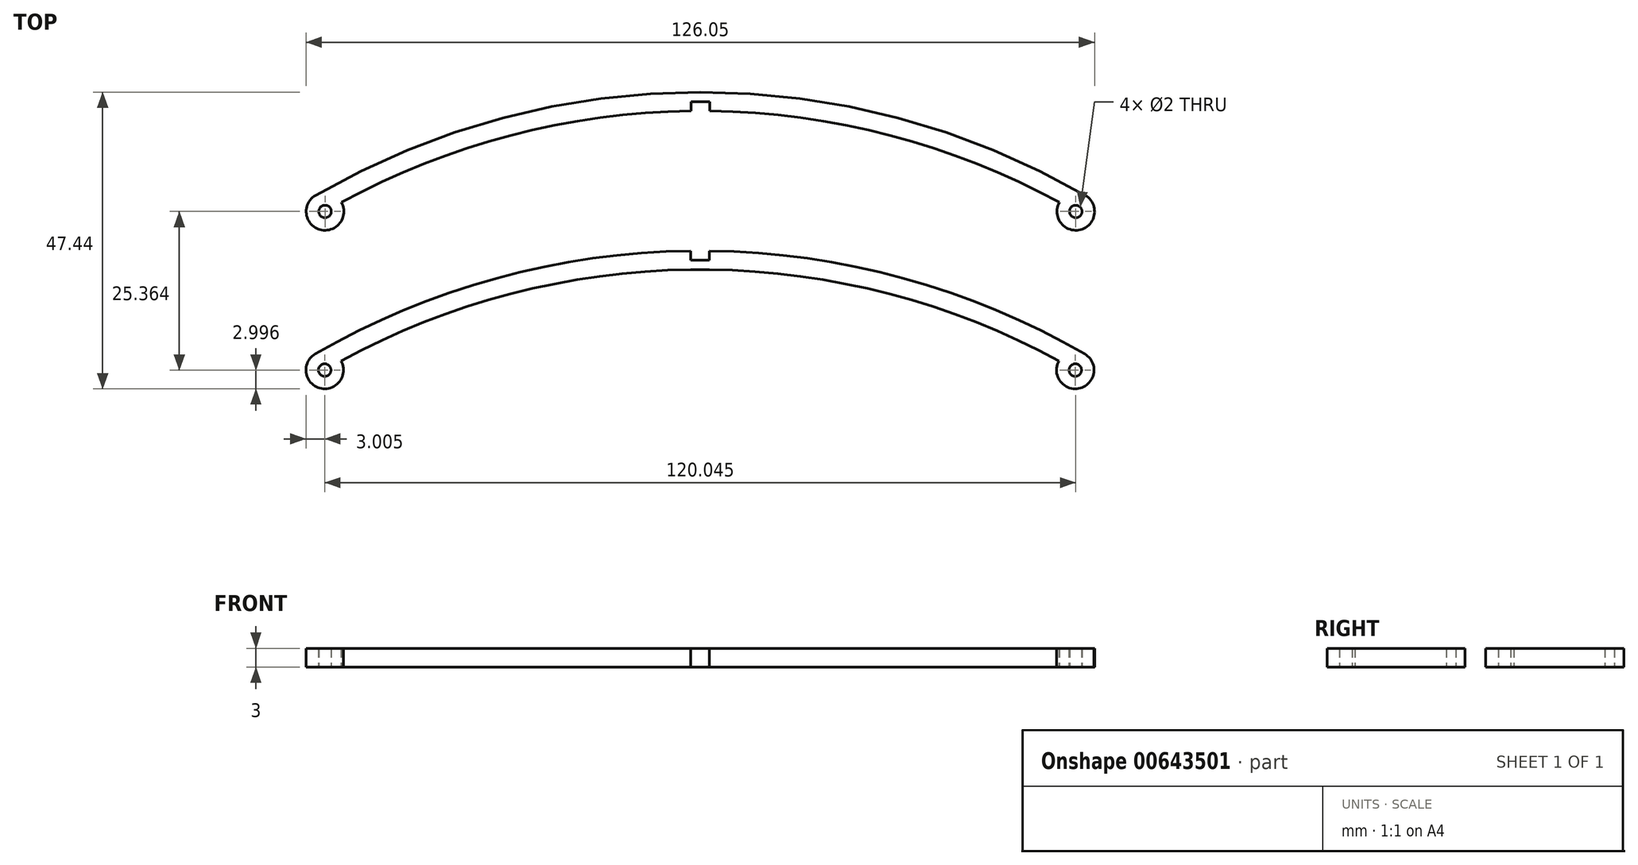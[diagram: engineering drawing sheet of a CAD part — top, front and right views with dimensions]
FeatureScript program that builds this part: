
annotation { "Feature Type Name" : "Feature", "Feature Type Description" : "" }
export const myFeature = defineFeature(function(context is Context, id is Id, definition is map)
    precondition{}
    {
        {
            var Q0;
            Q0=qCreatedBy(makeId("Top.planeOp"),FACE);
            var sketch = newSketch(context, id + "F0", { "sketchPlane" : qUnion([Q0])});
            skLineSegment(sketch, "E0", {"start": v(-60, 0) * mm, "end": v(60, 0) * mm, "construction": true});
            skArc(sketch, "E1.0", {"start": v(0, 19.08) * mm, "mid": v(-31.83, 14.89) * mm, "end": v(-61.5, 2.6) * mm});
            skLineSegment(sketch, "E2", {"start": v(-1.5, 17.57) * mm, "end": v(0, 17.57) * mm});
            skLineSegment(sketch, "E3", {"start": v(0, 0) * mm, "end": v(0, 24.5) * mm, "construction": true});
            skPoint(sketch, "E3.endSnap0", {"position": v(0, 16.08) * mm});
            skArc(sketch, "E4.trimOffspring", {"start": v(-1.5, 16.07) * mm, "mid": v(-30.33, 12.18) * mm, "end": v(-57.38, 1.47) * mm});
            skLineSegment(sketch, "E5", {"start": v(0, -17.99) * mm, "end": v(0, 6.51) * mm, "construction": true});
            skLineSegment(sketch, "E6", {"start": v(-1.5, 16.07) * mm, "end": v(-1.5, 17.57) * mm});
            skCircle(sketch, "E7", {"center": v(-60, 0) * mm, "radius": 1 * mm});
            skArc(sketch, "E8", {"start": v(-61.5, 2.6) * mm, "mid": v(-60.8, -2.9) * mm, "end": v(-57.38, 1.47) * mm});
            skCircle(sketch, "E9.MirrorC", {"center": v(60, 0) * mm, "radius": 1 * mm});
            skArc(sketch, "E10.MirrorCS", {"start": v(61.5, 2.6) * mm, "mid": v(60.8, -2.9) * mm, "end": v(57.38, 1.47) * mm});
            skArc(sketch, "E11.MirrorCS", {"start": v(0, 19.08) * mm, "mid": v(31.83, 14.89) * mm, "end": v(61.5, 2.6) * mm});
            skArc(sketch, "E12.MirrorCS", {"start": v(1.5, 16.07) * mm, "mid": v(30.33, 12.18) * mm, "end": v(57.38, 1.47) * mm});
            skLineSegment(sketch, "E13.MirrorCS", {"start": v(1.5, 17.57) * mm, "end": v(0, 17.57) * mm});
            skLineSegment(sketch, "E14.MirrorCS", {"start": v(1.5, 16.07) * mm, "end": v(1.5, 17.57) * mm});
            skLineSegment(sketch, "E15", {"start": v(-60.05, -25.36) * mm, "end": v(59.95, -25.36) * mm, "construction": true});
            skArc(sketch, "E16.0", {"start": v(-1.56, -6.3) * mm, "mid": v(-32.61, -10.68) * mm, "end": v(-61.55, -22.77) * mm});
            skLineSegment(sketch, "E17", {"start": v(-1.56, -7.8) * mm, "end": v(-0.06, -7.8) * mm});
            skLineSegment(sketch, "E18", {"start": v(-0.06, -25.36) * mm, "end": v(-0.06, -0.86) * mm, "construction": true});
            skPoint(sketch, "E18.endSnap0", {"position": v(-0.06, -9.29) * mm});
            skArc(sketch, "E19.trimOffspring", {"start": v(-1.56, -9.3) * mm, "mid": v(-30.39, -13.19) * mm, "end": v(-57.43, -23.9) * mm});
            skLineSegment(sketch, "E20", {"start": v(-0.06, -43.35) * mm, "end": v(-0.06, -18.85) * mm, "construction": true});
            skCircle(sketch, "E21", {"center": v(-60.05, -25.36) * mm, "radius": 1 * mm});
            skArc(sketch, "E22", {"start": v(-61.55, -22.77) * mm, "mid": v(-60.84, -28.26) * mm, "end": v(-57.43, -23.9) * mm});
            skCircle(sketch, "E23.MirrorC", {"center": v(59.92, -25.36) * mm, "radius": 1 * mm});
            skArc(sketch, "E24.MirrorCS", {"start": v(61.42, -22.77) * mm, "mid": v(60.71, -28.26) * mm, "end": v(57.3, -23.9) * mm});
            skArc(sketch, "E25.MirrorCS", {"start": v(-0.06, -6.29) * mm, "mid": v(-0.03, -6.29) * mm, "end": v(0, -6.29) * mm});
            skArc(sketch, "E26.MirrorCS", {"start": v(1.44, -9.3) * mm, "mid": v(30.26, -13.19) * mm, "end": v(57.3, -23.9) * mm});
            skLineSegment(sketch, "E27.MirrorCS", {"start": v(1.44, -7.8) * mm, "end": v(-0.06, -7.8) * mm});
            skLineSegment(sketch, "E28.MirrorCS", {"start": v(-1.56, -6.3) * mm, "end": v(-1.56, -7.8) * mm});
            skLineSegment(sketch, "E29.MirrorCS", {"start": v(1.44, -6.3) * mm, "end": v(1.44, -7.8) * mm});
            skLineSegment(sketch, "E30", {"start": v(-1.56, -9.3) * mm, "end": v(1.44, -9.3) * mm});
            skArc(sketch, "E31.trimOffspring", {"start": v(1.44, -6.3) * mm, "mid": v(32.48, -10.68) * mm, "end": v(61.42, -22.77) * mm});
            skPoint(sketch, "E32.orphan", {"position": v(-0.06, -6.29) * mm});
            skSolve(sketch);
        }
        {
            var Q0;
            Q0 = qSketchRegion(id + "F0", true);
            extrude(context, id + "F1", {"entities" : qUnion([Q0]), "depth" : 3 * mm, "offsetDistance" : 25 * mm});
        }
    });
